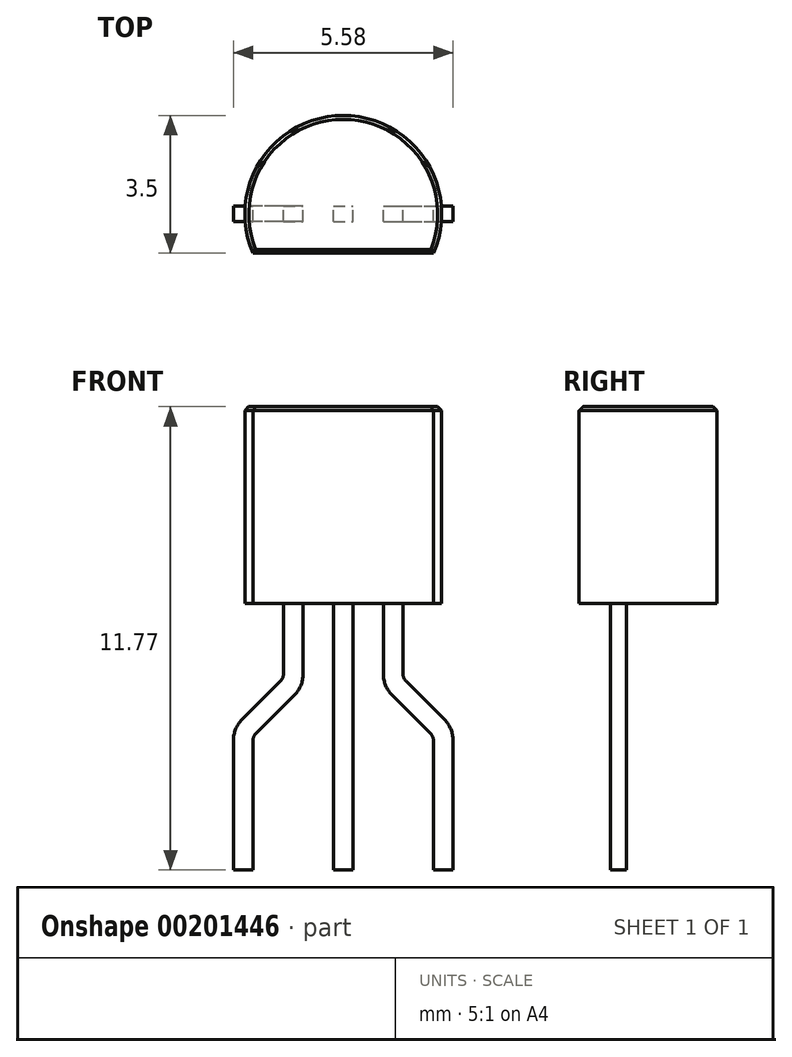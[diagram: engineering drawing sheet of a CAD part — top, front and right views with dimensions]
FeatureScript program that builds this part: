
annotation { "Feature Type Name" : "Feature", "Feature Type Description" : "" }
export const myFeature = defineFeature(function(context is Context, id is Id, definition is map)
    precondition{}
    {
        {
            var Q0;
            Q0=qCreatedBy(makeId("Top.planeOp"),FACE);
            var sketch = newSketch(context, id + "F0", { "sketchPlane" : qUnion([Q0])});
            skArc(sketch, "E0", {"start": v(2.3, -1) * mm, "mid": v(0, 2.5) * mm, "end": v(-2.3, -1) * mm});
            skLineSegment(sketch, "E1", {"start": v(-2.3, -1) * mm, "end": v(2.3, -1) * mm});
            skSolve(sketch);
        }
        {
            var Q0;
            Q0=makeQuery(id+"F0.imprint","IMPRINT",FACE,{"disambiguationData":[TD([[makeQuery(id+"F0.imprint","IMPRINT",EDGE,{"derivedFrom":sQuery(id+"F0.wireOp",EDGE,"E0")}),1.0]])]});
            extrude(context, id + "F1", {"entities" : qUnion([Q0]), "depth" : 5 * mm});
        }
        {
            var Q0;
            Q0=makeQuery(id+"F1.opExtrude","CAP_FACE",FACE,{"disambiguationData":[OSD([sQuery(id+"F0.wireOp",EDGE,"E0"),sQuery(id+"F0.wireOp",EDGE,"E1")])],"isStart":false});
            chamfer(context, id + "F2", {"entities" : qUnion([Q0]), "width" : 0.1 * mm, "tangentPropagation" : true});
        }
        {
            var Q0;
            Q0=makeQuery(id+"F1.opExtrude","CAP_FACE",FACE,{"disambiguationData":[OSD([sQuery(id+"F0.wireOp",EDGE,"E0"),sQuery(id+"F0.wireOp",EDGE,"E1")])],"isStart":true});
            var sketch = newSketch(context, id + "F3", { "sketchPlane" : qUnion([Q0])});
            skLineSegment(sketch, "E2.bottom", {"start": v(-1.52, 0.2) * mm, "end": v(-1.02, 0.2) * mm});
            skLineSegment(sketch, "E2.top", {"start": v(-1.52, -0.2) * mm, "end": v(-1.02, -0.2) * mm});
            skLineSegment(sketch, "E2.left", {"start": v(-1.52, 0.2) * mm, "end": v(-1.52, -0.2) * mm});
            skLineSegment(sketch, "E2.right", {"start": v(-1.02, 0.2) * mm, "end": v(-1.02, -0.2) * mm});
            skLineSegment(sketch, "E3", {"start": v(0, 1) * mm, "end": v(0, -2.5) * mm, "construction": true});
            skLineSegment(sketch, "E4", {"start": v(2.87, 0) * mm, "end": v(-2.9, 0) * mm, "construction": true});
            skLineSegment(sketch, "E5.bottom", {"start": v(-0.25, 0.2) * mm, "end": v(0.25, 0.2) * mm});
            skLineSegment(sketch, "E5.top", {"start": v(-0.25, -0.2) * mm, "end": v(0.25, -0.2) * mm});
            skLineSegment(sketch, "E5.left", {"start": v(-0.25, 0.2) * mm, "end": v(-0.25, -0.2) * mm});
            skLineSegment(sketch, "E5.right", {"start": v(0.25, 0.2) * mm, "end": v(0.25, -0.2) * mm});
            skLineSegment(sketch, "E6.bottom", {"start": v(1.02, 0.2) * mm, "end": v(1.52, 0.2) * mm});
            skLineSegment(sketch, "E6.top", {"start": v(1.02, -0.2) * mm, "end": v(1.52, -0.2) * mm});
            skLineSegment(sketch, "E6.left", {"start": v(1.02, 0.2) * mm, "end": v(1.02, -0.2) * mm});
            skLineSegment(sketch, "E6.right", {"start": v(1.52, 0.2) * mm, "end": v(1.52, -0.2) * mm});
            skLineSegment(sketch, "E7", {"start": v(-1.27, 0.5) * mm, "end": v(-1.27, -0.68) * mm, "construction": true});
            skLineSegment(sketch, "E8", {"start": v(1.27, 0.48) * mm, "end": v(1.27, -0.57) * mm, "construction": true});
            skSolve(sketch);
        }
        {
            var Q0;
            Q0=qCreatedBy(makeId("Front.planeOp"),FACE);
            var sketch = newSketch(context, id + "F4", { "sketchPlane" : qUnion([Q0])});
            skLineSegment(sketch, "E9", {"start": v(-2.94, 0) * mm, "end": v(2.94, 0) * mm, "construction": true});
            skLineSegment(sketch, "E10", {"start": v(0, -1.99) * mm, "end": v(0, 2.98) * mm, "construction": true});
            skLineSegment(sketch, "E11", {"start": v(0, 0) * mm, "end": v(0, -6.77) * mm});
            skLineSegment(sketch, "E12", {"start": v(-4.66, -6.77) * mm, "end": v(5.04, -6.77) * mm, "construction": true});
            skLineSegment(sketch, "E13", {"start": v(1.27, 0) * mm, "end": v(1.27, -1.8) * mm});
            skLineSegment(sketch, "E14", {"start": v(2.54, -3.48) * mm, "end": v(2.54, -6.77) * mm});
            skLineSegment(sketch, "E15", {"start": v(1.42, -2.15) * mm, "end": v(2.4, -3.12) * mm});
            skPoint(sketch, "E16.visualSharp", {"position": v(1.27, -2) * mm});
            skArc(sketch, "E16.filletArc", {"start": v(1.27, -1.8) * mm, "mid": v(1.3, -1.98) * mm, "end": v(1.42, -2.15) * mm});
            skPoint(sketch, "E17.visualSharp", {"position": v(2.54, -3.27) * mm});
            skArc(sketch, "E17.filletArc", {"start": v(2.54, -3.48) * mm, "mid": v(2.5, -3.29) * mm, "end": v(2.4, -3.12) * mm});
            skLineSegment(sketch, "E18.MirrorCS", {"start": v(-1.27, 0) * mm, "end": v(-1.27, -1.8) * mm});
            skArc(sketch, "E19.MirrorCS", {"start": v(-1.27, -1.8) * mm, "mid": v(-1.3, -1.98) * mm, "end": v(-1.42, -2.15) * mm});
            skLineSegment(sketch, "E20.MirrorCS", {"start": v(-1.42, -2.15) * mm, "end": v(-2.4, -3.12) * mm});
            skArc(sketch, "E21.MirrorCS", {"start": v(-2.54, -3.48) * mm, "mid": v(-2.5, -3.29) * mm, "end": v(-2.4, -3.12) * mm});
            skLineSegment(sketch, "E22.MirrorCS", {"start": v(-2.54, -3.48) * mm, "end": v(-2.54, -6.77) * mm});
            skSolve(sketch);
        }
        {
            var Q0;
            Q0=makeQuery(id+"F3.imprint","IMPRINT",FACE,{"disambiguationData":[TD([[makeQuery(id+"F3.imprint","IMPRINT",EDGE,{"derivedFrom":sQuery(id+"F3.wireOp",EDGE,"E2.bottom")}),-1.0]])]});
            var Q1;
            Q1=sQuery(id+"F4.wireOp",EDGE,"E18.MirrorCS");
            var Q2;
            Q2=sQuery(id+"F4.wireOp",EDGE,"E19.MirrorCS");
            var Q3;
            Q3=sQuery(id+"F4.wireOp",EDGE,"E20.MirrorCS");
            var Q4;
            Q4=sQuery(id+"F4.wireOp",EDGE,"E22.MirrorCS");
            var Q5;
            Q5=sQuery(id+"F4.wireOp",EDGE,"E21.MirrorCS");
            sweep(context, id + "F5", {"operationType" : NewBodyOperationType.ADD, "profiles" : qUnion([Q0]), "path" : qUnion([Q1, Q2, Q3, Q4, Q5])});
        }
        {
            var Q0;
            Q0=makeQuery(id+"F3.imprint","IMPRINT",FACE,{"disambiguationData":[TD([[makeQuery(id+"F3.imprint","IMPRINT",EDGE,{"derivedFrom":sQuery(id+"F3.wireOp",EDGE,"E5.bottom")}),-1.0]])]});
            var Q1;
            Q1=sQuery(id+"F4.wireOp",EDGE,"E11");
            sweep(context, id + "F6", {"operationType" : NewBodyOperationType.ADD, "profiles" : qUnion([Q0]), "path" : qUnion([Q1])});
        }
        {
            var Q0;
            Q0=makeQuery(id+"F3.imprint","IMPRINT",FACE,{"disambiguationData":[TD([[makeQuery(id+"F3.imprint","IMPRINT",EDGE,{"derivedFrom":sQuery(id+"F3.wireOp",EDGE,"E6.bottom")}),-1.0]])]});
            var Q1;
            Q1=sQuery(id+"F4.wireOp",EDGE,"E13");
            var Q2;
            Q2=sQuery(id+"F4.wireOp",EDGE,"E16.filletArc");
            var Q3;
            Q3=sQuery(id+"F4.wireOp",EDGE,"E15");
            var Q4;
            Q4=sQuery(id+"F4.wireOp",EDGE,"E17.filletArc");
            var Q5;
            Q5=sQuery(id+"F4.wireOp",EDGE,"E14");
            sweep(context, id + "F7", {"operationType" : NewBodyOperationType.ADD, "profiles" : qUnion([Q0]), "path" : qUnion([Q1, Q2, Q3, Q4, Q5])});
        }
    });
